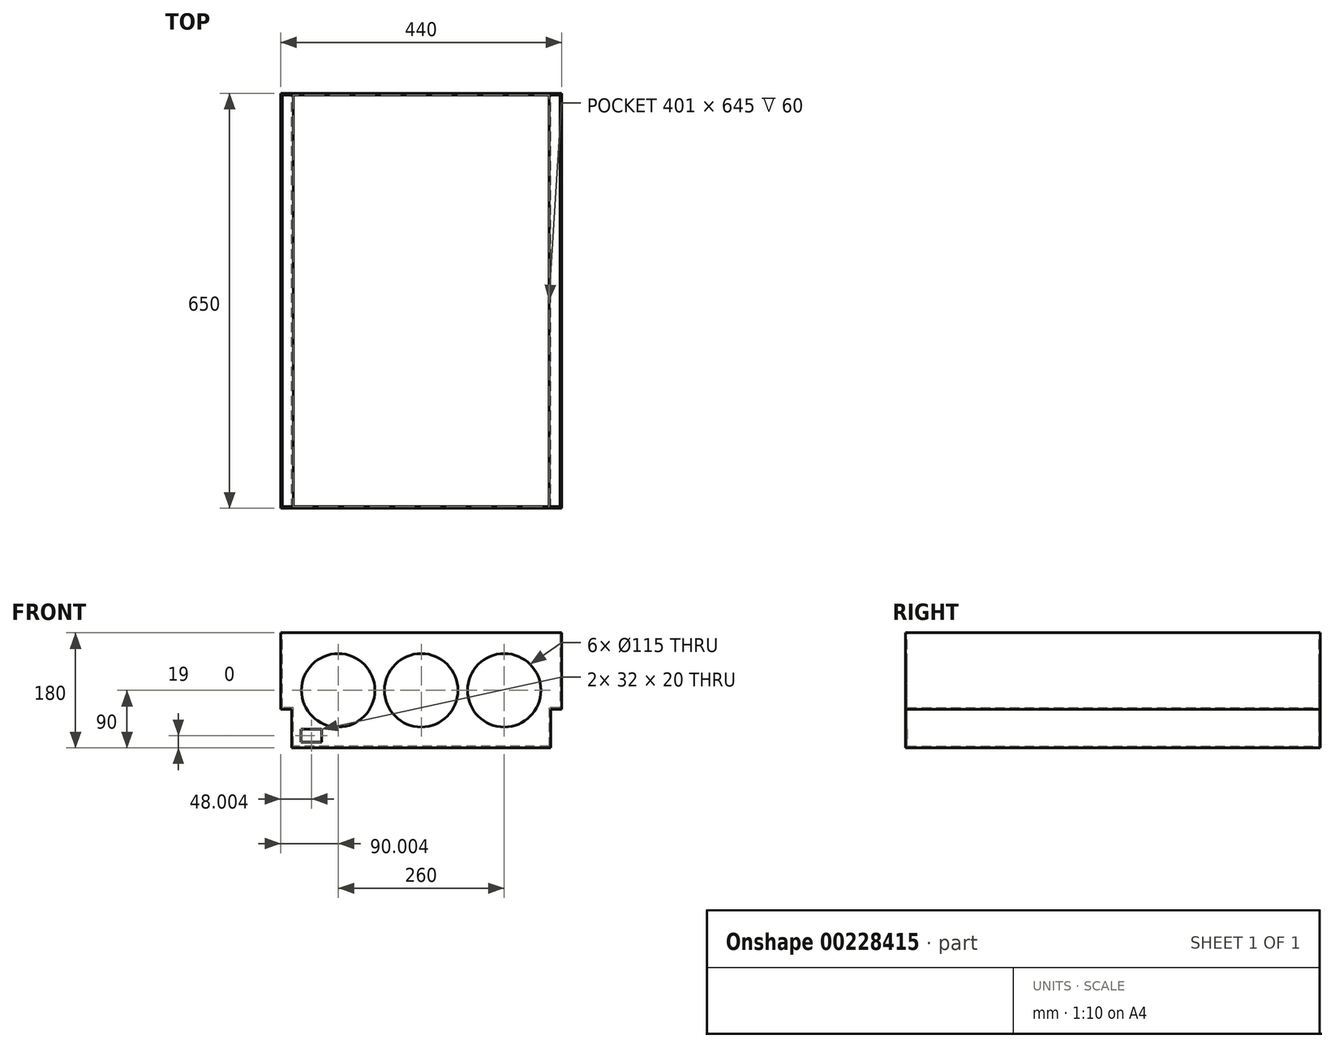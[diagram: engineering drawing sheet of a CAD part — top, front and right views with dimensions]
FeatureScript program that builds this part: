
annotation { "Feature Type Name" : "Feature", "Feature Type Description" : "" }
export const myFeature = defineFeature(function(context is Context, id is Id, definition is map)
    precondition{}
    {
        {
            var Q0;
            Q0=qCreatedBy(makeId("Front.planeOp"),FACE);
            var sketch = newSketch(context, id + "F0", { "sketchPlane" : qUnion([Q0])});
            skLineSegment(sketch, "E0", {"start": v(-222.14, 95.57) * mm, "end": v(217.86, 95.57) * mm});
            skLineSegment(sketch, "E1", {"start": v(217.86, 95.57) * mm, "end": v(217.86, -24.43) * mm});
            skLineSegment(sketch, "E2", {"start": v(217.86, -24.43) * mm, "end": v(200.86, -24.43) * mm});
            skLineSegment(sketch, "E3", {"start": v(200.86, -24.43) * mm, "end": v(200.86, -84.43) * mm});
            skLineSegment(sketch, "E4", {"start": v(200.86, -84.43) * mm, "end": v(-205.14, -84.43) * mm});
            skLineSegment(sketch, "E5", {"start": v(-205.14, -84.43) * mm, "end": v(-205.14, -24.43) * mm});
            skLineSegment(sketch, "E6", {"start": v(-205.14, -24.43) * mm, "end": v(-222.14, -24.43) * mm});
            skLineSegment(sketch, "E7", {"start": v(-222.14, -24.43) * mm, "end": v(-222.14, 95.57) * mm});
            skPoint(sketch, "E8", {"position": v(127.86, 5.57) * mm});
            skPoint(sketch, "E9", {"position": v(-2.14, 5.57) * mm});
            skPoint(sketch, "E10", {"position": v(-132.14, 5.57) * mm});
            skLineSegment(sketch, "E11.bottom", {"start": v(-190.14, -55.43) * mm, "end": v(-158.14, -55.43) * mm});
            skLineSegment(sketch, "E11.top", {"start": v(-190.14, -75.43) * mm, "end": v(-158.14, -75.43) * mm});
            skLineSegment(sketch, "E11.left", {"start": v(-190.14, -55.43) * mm, "end": v(-190.14, -75.43) * mm});
            skLineSegment(sketch, "E11.right", {"start": v(-158.14, -55.43) * mm, "end": v(-158.14, -75.43) * mm});
            skSolve(sketch);
        }
        {
            var Q0;
            Q0=makeQuery(id+"F0.imprint","IMPRINT",FACE,{"disambiguationData":[TD([[makeQuery(id+"F0.imprint","IMPRINT",EDGE,{"derivedFrom":sQuery(id+"F0.wireOp",EDGE,"E0")}),-1.0]])]});
            extrude(context, id + "F1", {"entities" : qUnion([Q0]), "depth" : 650 * mm});
        }
        {
            var Q0;
            Q0=makeQuery(id+"F1.opExtrude","SWEPT_FACE",FACE,{"disambiguationData":[OSD([sQuery(id+"F0.wireOp",EDGE,"E0")])]});
            shell(context, id + "F2", {"entities" : qUnion([Q0]), "thickness" : 2.5 * mm});
        }
        {
            var Q0;
            Q0=sQuery(id+"F0.wireOp",VERTEX,"E10");
            var Q1;
            Q1=sQuery(id+"F0.wireOp",VERTEX,"E9");
            var Q2;
            Q2=sQuery(id+"F0.wireOp",VERTEX,"E8");
            var Q3;
            Q3=makeQuery(id+"F1.opExtrude","SWEPT_BODY",BODY,{"disambiguationData":[OSD([sQuery(id+"F0.wireOp",EDGE,"E0"),sQuery(id+"F0.wireOp",EDGE,"E1"),sQuery(id+"F0.wireOp",EDGE,"E2"),sQuery(id+"F0.wireOp",EDGE,"E3"),sQuery(id+"F0.wireOp",EDGE,"E4"),sQuery(id+"F0.wireOp",EDGE,"E5"),sQuery(id+"F0.wireOp",EDGE,"E6"),sQuery(id+"F0.wireOp",EDGE,"E7")])]});
            hole(context, id + "F3", {"style" : HoleStyle.SIMPLE, "endStyle" : HoleEndStyle.THROUGH, "oppositeDirection" : true, "holeDiameter" : 115 * mm, "locations" : qUnion([Q0, Q1, Q2]), "scope" : qUnion([Q3]), "isTappedThrough" : true});
        }
        {
            var Q0;
            Q0=makeQuery(id+"F2.opShell","OFFSET_FACE",FACE,{"disambiguationData":[OSD([sQuery(id+"F0.wireOp",EDGE,"E11.bottom")])]});
            extrude(context, id + "F4", {"entities" : qUnion([Q0]), "operationType" : NewBodyOperationType.REMOVE, "oppositeDirection" : true, "depth" : 25 * mm});
        }
    });
